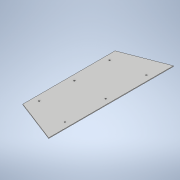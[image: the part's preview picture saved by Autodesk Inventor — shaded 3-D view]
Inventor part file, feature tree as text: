
AUTODESK INVENTOR PART (.ipt)
format: ipt  version: 2021 (Build 250183000, 183)  size: 119,808 bytes
history: native  units: in
note: dims shown in document units (in); Inventor stores cm internally (conversion verified against a paired STEP export)
features: extrude x1, sketch x1
ambient origin geometry x8: Origin, YZ Plane, XZ Plane, XY Plane, X Axis, Y Axis, Z Axis, Center Point
bodies: Solid1 (feature_tree)
feature tree (2):
  extrude  "Extrusion1"  Depth=11.5in
  sketch  "Sketch1"  dims[d0=11.5in d1=11.5in d2=7.76in d3=8.5in d4=8.5in d5=0.125in d6=0.0in d7=2.0in d8=1.0in d9=0.25in d10=4.0in d11=4.0in d12=1.0in d13=1.0in d14=1.0in d15=1.0in d16=0.25in d17=0.25in d18=2.0in d19=1.0in d20=0.25in d21=0.25in d22=0.25in]
